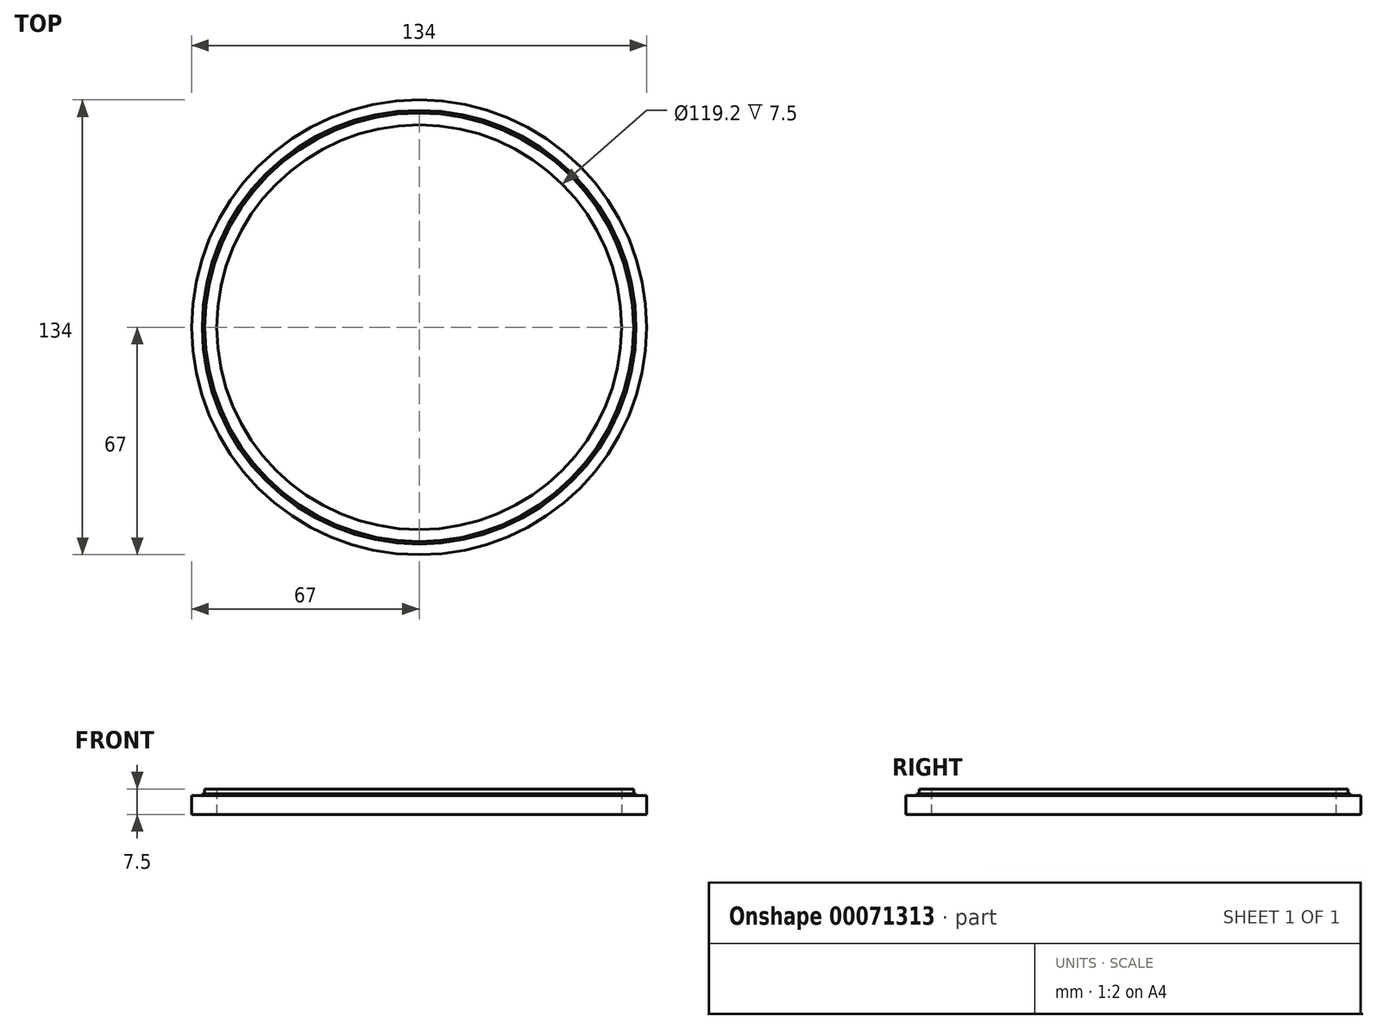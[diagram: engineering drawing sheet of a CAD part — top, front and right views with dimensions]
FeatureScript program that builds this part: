
annotation { "Feature Type Name" : "Feature", "Feature Type Description" : "" }
export const myFeature = defineFeature(function(context is Context, id is Id, definition is map)
    precondition{}
    {
        {
            var Q0;
            Q0=qCreatedBy(makeId("Top.planeOp"),FACE);
            var sketch = newSketch(context, id + "F0", { "sketchPlane" : qUnion([Q0])});
            skCircle(sketch, "E0", {"center": v(0, 0) * mm, "radius": 59.6 * mm});
            skCircle(sketch, "E1", {"center": v(0, 0) * mm, "radius": 67 * mm});
            skSolve(sketch);
        }
        {
            var Q0;
            Q0=makeQuery(id+"F0.imprint","IMPRINT",FACE,{"disambiguationData":[TD([[makeQuery(id+"F0.imprint","IMPRINT",EDGE,{"derivedFrom":sQuery(id+"F0.wireOp",EDGE,"E0")}),-1.0]])]});
            extrude(context, id + "F1", {"entities" : qUnion([Q0]), "endBound" : BoundingType.SYMMETRIC, "depth" : 7.5 * mm});
        }
        {
            var Q0;
            Q0=makeQuery(id+"F1.opExtrude","CAP_FACE",FACE,{"disambiguationData":[OSD([sQuery(id+"F0.wireOp",EDGE,"E0"),sQuery(id+"F0.wireOp",EDGE,"E1")])],"isStart":false});
            var sketch = newSketch(context, id + "F2", { "sketchPlane" : qUnion([Q0])});
            skCircle(sketch, "E2", {"center": v(0, 0) * mm, "radius": 63.12 * mm});
            skCircle(sketch, "E3", {"center": v(0, 0) * mm, "radius": 63.88 * mm});
            skSolve(sketch);
        }
        {
            var Q0;
            Q0=makeQuery(id+"F2.imprint","IMPRINT",FACE,{"disambiguationData":[TD([[makeQuery(id+"F2.imprint","IMPRINT",EDGE,{"derivedFrom":sQuery(id+"F2.wireOp",EDGE,"E2")}),-1.0]])]});
            extrude(context, id + "F3", {"entities" : qUnion([Q0]), "operationType" : NewBodyOperationType.REMOVE, "oppositeDirection" : true, "depth" : 1.5 * mm});
        }
        {
            var Q0;
            {var subQ0=sQuery(id+"F0.wireOp",EDGE,"E1");Q0=makeQuery(id+"F3.boolean.opBoolean","SPLIT",FACE,{"disambiguationData":[TD([makeQuery(id+"F1.opExtrude","SWEPT_FACE",FACE,{"disambiguationData":[OSD([subQ0])]})])],"derivedFrom":makeQuery(id+"F1.opExtrude","CAP_FACE",FACE,{"disambiguationData":[OSD([sQuery(id+"F0.wireOp",EDGE,"E0"),subQ0])],"isStart":false})});}
            extrude(context, id + "F4", {"entities" : qUnion([Q0]), "operationType" : NewBodyOperationType.REMOVE, "oppositeDirection" : true, "depth" : 2 * mm});
        }
    });
